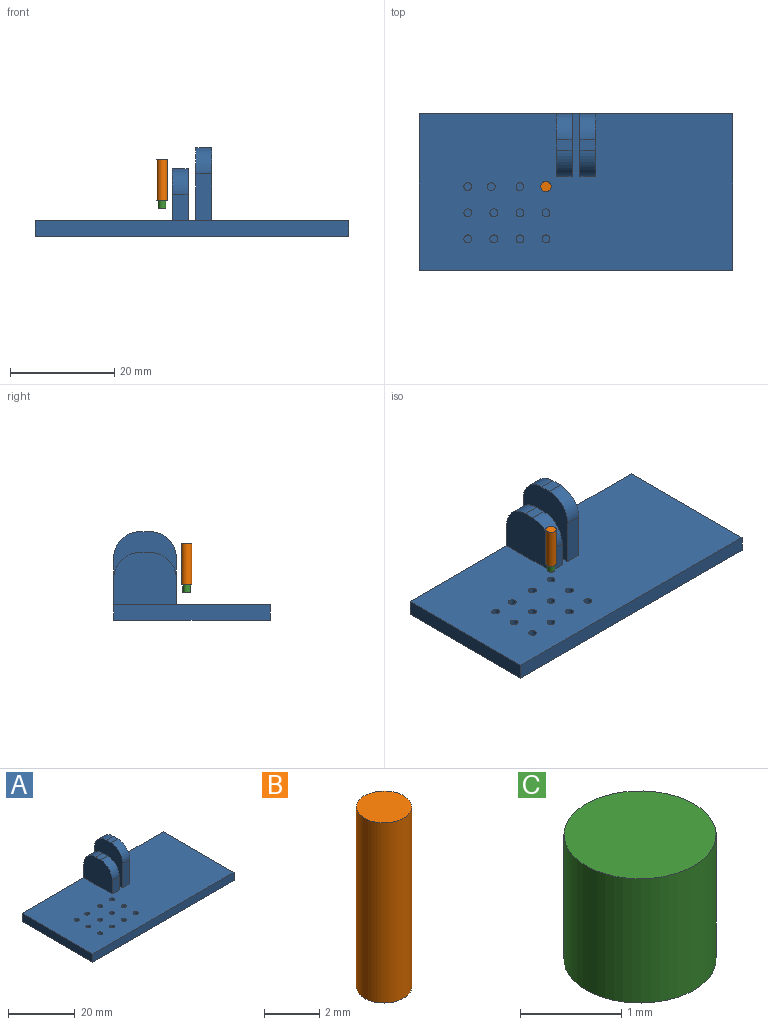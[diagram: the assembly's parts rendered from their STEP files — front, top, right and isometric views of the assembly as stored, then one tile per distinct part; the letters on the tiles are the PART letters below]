
ASSEMBLY  parts=3 mates=2
PART A: 42 faces, bbox 60x30x17 mm
  f0: plane 60x30mm, normal (0,0,1), area 1706.8mm2, adj f1,f2,f3,f4,f6,f7,f8,f9
  f1: plane 60x3mm, normal (0,-1,0), area 180mm2, adj f0,f2,f4,f5
  f2: plane 30x3mm, normal (1,0,0), area 90mm2, adj f0,f1,f3,f5
  f3: plane 60x12mm, normal (0,1,0), area 222mm2, adj f0,f2,f4,f5,f6,f8,f9,f10
  f4: plane 30x3mm, normal (-1,0,0), area 90mm2, adj f0,f1,f3,f5
  f5: plane 60x30mm, normal (0,0,-1), area 1800mm2, adj f1,f2,f3,f4
  f6: plane 14x12mm, normal (-1,0,0), area 157.3mm2, adj f0,f3,f7,f13,f14,f15
  f7: plane 9x3mm, normal (0,-1,0), area 27mm2, adj f0,f6,f8,f15
  f8: plane 14x12mm, normal (1,0,0), area 157.3mm2, adj f0,f3,f7,f13,f14,f15
  f9: plane 12x10mm, normal (1,0,0), area 109.3mm2, adj f0,f3,f11,f12,f16,f17
  f10: plane 12x10mm, normal (-1,0,0), area 109.3mm2, adj f0,f3,f11,f12,f16,f17
  f11: plane 5x3mm, normal (0,-1,0), area 15mm2, adj f0,f9,f10,f17
  f12: plane 3x2mm, normal (0,0,1), area 6mm2, adj f9,f10,f16,f17
  f13: plane 3x2mm, normal (0,0,1), area 6mm2, adj f6,f8,f14,f15
  f14: cylinder r=5mm len=5mm, axis (1,0,0), area 23.6mm2, adj f3,f6,f8,f13
  f15: cylinder r=5mm len=5mm, axis (-1,0,0), area 23.6mm2, adj f6,f7,f8,f13
  f16: cylinder r=5mm len=5mm, axis (1,0,0), area 23.6mm2, adj f3,f9,f10,f12
  f17: cylinder r=5mm len=5mm, axis (-1,0,0), area 23.6mm2, adj f9,f10,f11,f12
  f18: cylinder r=0.75mm len=1.5mm, axis (0,0,1), area 7.1mm2, adj f0,f19
  f19: plane 1.5x1.5mm, normal (0,0,1), area 1.8mm2, adj f18
  f20: cylinder r=0.75mm len=1.5mm, axis (0,0,1), area 7.1mm2, adj f0,f21
  f21: plane 1.5x1.5mm, normal (0,0,1), area 1.8mm2, adj f20
  f22: cylinder r=0.75mm len=1.5mm, axis (0,0,1), area 7.1mm2, adj f0,f23
  f23: plane 1.5x1.5mm, normal (0,0,1), area 1.8mm2, adj f22
  f24: cylinder r=0.75mm len=1.5mm, axis (0,0,1), area 7.1mm2, adj f0,f25
  f25: plane 1.5x1.5mm, normal (0,0,1), area 1.8mm2, adj f24
  f26: cylinder r=0.75mm len=1.5mm, axis (0,0,1), area 7.1mm2, adj f0,f27
  f27: plane 1.5x1.5mm, normal (0,0,1), area 1.8mm2, adj f26
  f28: cylinder r=0.75mm len=1.5mm, axis (0,0,1), area 7.1mm2, adj f0,f29
  f29: plane 1.5x1.5mm, normal (0,0,1), area 1.8mm2, adj f28
  f30: cylinder r=0.75mm len=1.5mm, axis (0,0,1), area 7.1mm2, adj f0,f31
  f31: plane 1.5x1.5mm, normal (0,0,1), area 1.8mm2, adj f30
  f32: cylinder r=0.75mm len=1.5mm, axis (0,0,1), area 7.1mm2, adj f0,f33
  f33: plane 1.5x1.5mm, normal (0,0,1), area 1.8mm2, adj f32
  f34: cylinder r=0.75mm len=1.5mm, axis (0,0,1), area 7.1mm2, adj f0,f35
  f35: plane 1.5x1.5mm, normal (0,0,1), area 1.8mm2, adj f34
  f36: cylinder r=0.75mm len=1.5mm, axis (0,0,1), area 7.1mm2, adj f0,f37
  f37: plane 1.5x1.5mm, normal (0,0,1), area 1.8mm2, adj f36
  f38: cylinder r=0.75mm len=1.5mm, axis (0,0,1), area 7.1mm2, adj f0,f39
  f39: plane 1.5x1.5mm, normal (0,0,1), area 1.8mm2, adj f38
  f40: cylinder r=0.75mm len=1.5mm, axis (0,0,1), area 7.1mm2, adj f0,f41
  f41: plane 1.5x1.5mm, normal (0,0,1), area 1.8mm2, adj f40
PART B: 3 faces, bbox 2x2x8 mm
  f0: cylinder r=1mm len=8mm, axis (0,0,-1), area 50.3mm2, adj f1,f2
  f1: plane 2x2mm, normal (0,0,1), area 3.1mm2, adj f0
  f2: plane 2x2mm, normal (0,0,-1), area 3.1mm2, adj f0
PART C: 3 faces, bbox 1.5x1.5x1.5 mm
  f0: cylinder r=0.75mm len=1.5mm, axis (0,0,-1), area 7.1mm2, adj f1,f2
  f1: plane 1.5x1.5mm, normal (0,0,1), area 1.8mm2, adj f0
  f2: plane 1.5x1.5mm, normal (0,0,-1), area 1.8mm2, adj f0
PLACE A t=(-11.4,9.04,-1.54)mm
PLACE B t=(-17.15,10.07,3.75)mm
PLACE C t=(-17.15,10.07,3.75)mm
MATE fastened C.f0 <-> B.f0  axis (0,0,1) through (-17.15,10.07,5.25)mm
MATE slider A.f28 <-> C.f0  axis (0,0,1) through (-17.15,10.07,1.46)mm
